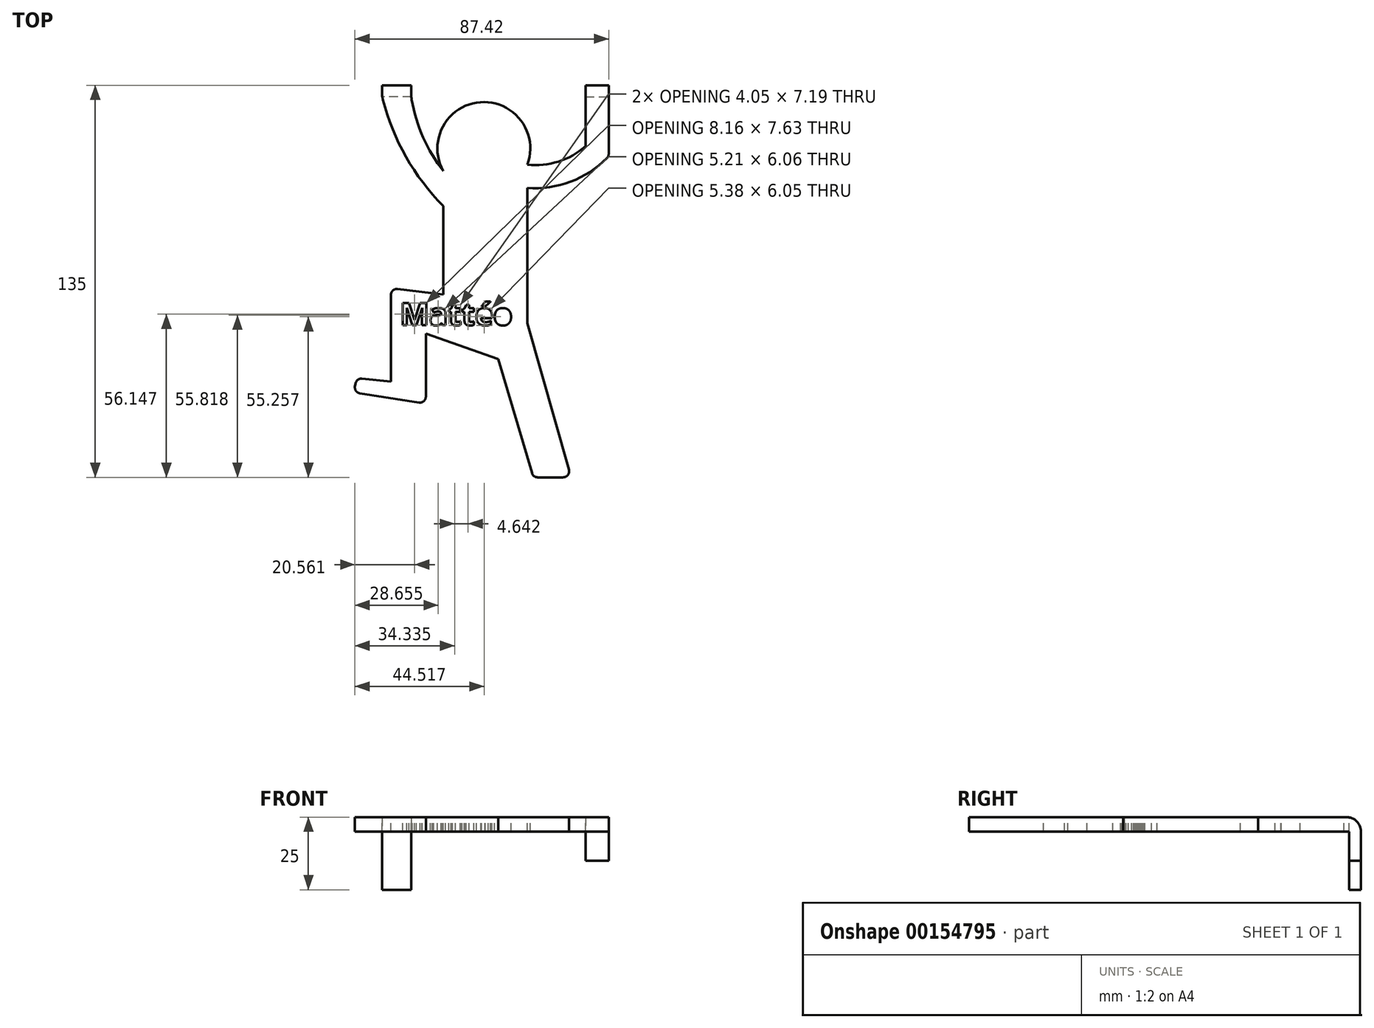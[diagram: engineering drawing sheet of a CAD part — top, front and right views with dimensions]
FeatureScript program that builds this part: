
annotation { "Feature Type Name" : "Feature", "Feature Type Description" : "" }
export const myFeature = defineFeature(function(context is Context, id is Id, definition is map)
    precondition{}
    {
        {
            var Q0;
            Q0=qCreatedBy(makeId("Top.planeOp"),FACE);
            var sketch = newSketch(context, id + "F0", { "sketchPlane" : qUnion([Q0])});
            skCircle(sketch, "E0", {"center": v(0, 33.2) * mm, "radius": 16 * mm});
            skLineSegment(sketch, "E1", {"start": v(15, 19.62) * mm, "end": v(15, -26.94) * mm});
            skLineSegment(sketch, "E2", {"start": v(15, -26.94) * mm, "end": v(30, -80) * mm});
            skLineSegment(sketch, "E3", {"start": v(30, -80) * mm, "end": v(17, -80) * mm});
            skLineSegment(sketch, "E4", {"start": v(17, -80) * mm, "end": v(5, -39.34) * mm});
            skLineSegment(sketch, "E5", {"start": v(5, -39.34) * mm, "end": v(-20, -30.5) * mm});
            skLineSegment(sketch, "E6", {"start": v(-20, -30.5) * mm, "end": v(-20, -54.61) * mm});
            skLineSegment(sketch, "E7", {"start": v(-20, -54.61) * mm, "end": v(-44.7, -50.77) * mm});
            skLineSegment(sketch, "E8", {"start": v(-44.7, -50.77) * mm, "end": v(-43.94, -45.83) * mm});
            skLineSegment(sketch, "E9", {"start": v(-43.94, -45.83) * mm, "end": v(-32, -47.08) * mm});
            skLineSegment(sketch, "E10", {"start": v(-32, -47.08) * mm, "end": v(-32, -14.9) * mm});
            skLineSegment(sketch, "E11", {"start": v(-32, -14.9) * mm, "end": v(-14, -17.13) * mm});
            skLineSegment(sketch, "E12", {"start": v(-14, -17.13) * mm, "end": v(-14, 13.45) * mm});
            skLineSegment(sketch, "E13.bottom", {"start": v(35, 55) * mm, "end": v(43, 55) * mm});
            skLineSegment(sketch, "E13.top", {"start": v(35, 51) * mm, "end": v(43, 51) * mm});
            skLineSegment(sketch, "E13.left", {"start": v(35, 55) * mm, "end": v(35, 51) * mm});
            skLineSegment(sketch, "E13.right", {"start": v(43, 55) * mm, "end": v(43, 51) * mm});
            skLineSegment(sketch, "E14.bottom", {"start": v(-25, 55) * mm, "end": v(-35, 55) * mm});
            skLineSegment(sketch, "E14.top", {"start": v(-25, 51) * mm, "end": v(-35, 51) * mm});
            skLineSegment(sketch, "E14.left", {"start": v(-25, 55) * mm, "end": v(-25, 51) * mm});
            skLineSegment(sketch, "E14.right", {"start": v(-35, 55) * mm, "end": v(-35, 51) * mm});
            skPoint(sketch, "E15", {"position": v(-14, 25.45) * mm});
            skPoint(sketch, "E16", {"position": v(15, 19.62) * mm});
            skPoint(sketch, "E17", {"position": v(15, 27.62) * mm});
            skArc(sketch, "E18", {"start": v(-25, 51) * mm, "mid": v(-21.14, 37.52) * mm, "end": v(-14, 25.45) * mm});
            skArc(sketch, "E19", {"start": v(-35, 51) * mm, "mid": v(-27.07, 30.78) * mm, "end": v(-14, 13.45) * mm});
            skLineSegment(sketch, "E20", {"start": v(43, 51) * mm, "end": v(43, 30.54) * mm});
            skLineSegment(sketch, "E21", {"start": v(35, 51) * mm, "end": v(35, 34) * mm});
            skArc(sketch, "E22", {"start": v(15, 19.62) * mm, "mid": v(30.23, 21.92) * mm, "end": v(43, 30.54) * mm});
            skArc(sketch, "E23", {"start": v(15, 27.62) * mm, "mid": v(25.67, 28.7) * mm, "end": v(35, 34) * mm});
            skText(sketch, "E24", { "text": "Mattéo", "fontName": "OpenSans-Bold.ttf"});
            const initialGuessF0  = {"E24": [-0.0289, -0.02767, 1, 0, 0.0077]};
            skSetInitialGuess(sketch, initialGuessF0);
            skSolve(sketch);
        }
        {
            var Q0;
            Q0=makeQuery(id+"F0.imprint","IMPRINT",FACE,{"disambiguationData":[TD([[makeQuery(id+"F0.imprint","IMPRINT",EDGE,{"derivedFrom":sQuery(id+"F0.wireOp",EDGE,"E1")}),-1.0]])]});
            var Q1;
            {var subQ0=sQuery(id+"F0.wireOp",EDGE,"E0");var subQ1=makeQuery(id+"F0.imprint","INTERSECT",VERTEX,{"derivedFrom":[subQ0,sQuery(id+"F0.wireOp",EDGE,"E18")]});Q1=makeQuery(id+"F0.imprint","IMPRINT",FACE,{"disambiguationData":[TD([[makeQuery(id+"F0.imprint","IMPRINT",EDGE,{"disambiguationData":[TD([[subQ1,-1.0]])],"derivedFrom":subQ0}),1.0]])]});}
            extrude(context, id + "F1", {"entities" : qUnion([Q0, Q1]), "oppositeDirection" : true, "depth" : 5 * mm});
        }
        {
            var Q0;
            Q0=makeQuery(id+"F0.imprint","IMPRINT",FACE,{"disambiguationData":[TD([[makeQuery(id+"F0.imprint","IMPRINT",EDGE,{"derivedFrom":sQuery(id+"F0.wireOp",EDGE,"E14.bottom")}),1.0]])]});
            extrude(context, id + "F2", {"entities" : qUnion([Q0]), "operationType" : NewBodyOperationType.ADD, "oppositeDirection" : true, "depth" : 25 * mm});
        }
        {
            var Q0;
            Q0=makeQuery(id+"F0.imprint","IMPRINT",FACE,{"disambiguationData":[TD([[makeQuery(id+"F0.imprint","IMPRINT",EDGE,{"derivedFrom":sQuery(id+"F0.wireOp",EDGE,"E13.bottom")}),-1.0]])]});
            extrude(context, id + "F3", {"entities" : qUnion([Q0]), "operationType" : NewBodyOperationType.ADD, "oppositeDirection" : true, "depth" : 15 * mm});
        }
        {
            var Q0;
            Q0=makeQuery(id+"F2.opExtrude","CAP_EDGE",EDGE,{"disambiguationData":[OSD([sQuery(id+"F0.wireOp",EDGE,"E14.bottom")])],"isStart":true});
            var Q1;
            Q1=makeQuery(id+"F3.opExtrude","CAP_EDGE",EDGE,{"disambiguationData":[OSD([sQuery(id+"F0.wireOp",EDGE,"E13.bottom")])],"isStart":true});
            fillet(context, id + "F4", {"entities" : qUnion([Q0, Q1]), "radius" : 5 * mm, "tangentPropagation" : true, "allowEdgeOverflow" : false});
        }
        {
            var Q0;
            Q0=makeQuery(id+"F1.opExtrude","SWEPT_EDGE",EDGE,{"disambiguationData":[OSD([sQuery(id+"F0.wireOp",EDGE,"E8"),sQuery(id+"F0.wireOp",EDGE,"E9")])]});
            var Q1;
            Q1=makeQuery(id+"F1.opExtrude","SWEPT_EDGE",EDGE,{"disambiguationData":[OSD([sQuery(id+"F0.wireOp",EDGE,"E7"),sQuery(id+"F0.wireOp",EDGE,"E8")])]});
            var Q2;
            Q2=makeQuery(id+"F1.opExtrude","SWEPT_EDGE",EDGE,{"disambiguationData":[OSD([sQuery(id+"F0.wireOp",EDGE,"E3"),sQuery(id+"F0.wireOp",EDGE,"E4")])]});
            var Q3;
            Q3=makeQuery(id+"F1.opExtrude","SWEPT_EDGE",EDGE,{"disambiguationData":[OSD([sQuery(id+"F0.wireOp",EDGE,"E2"),sQuery(id+"F0.wireOp",EDGE,"E3")])]});
            var Q4;
            Q4=makeQuery(id+"F1.opExtrude","SWEPT_EDGE",EDGE,{"disambiguationData":[OSD([sQuery(id+"F0.wireOp",EDGE,"E6"),sQuery(id+"F0.wireOp",EDGE,"E7")])]});
            var Q5;
            Q5=makeQuery(id+"F1.opExtrude","SWEPT_EDGE",EDGE,{"disambiguationData":[OSD([sQuery(id+"F0.wireOp",EDGE,"E10"),sQuery(id+"F0.wireOp",EDGE,"E11")])]});
            var Q6;
            Q6=makeQuery(id+"F1.opExtrude","SWEPT_EDGE",EDGE,{"disambiguationData":[OSD([sQuery(id+"F0.wireOp",EDGE,"E20"),sQuery(id+"F0.wireOp",EDGE,"E22")])]});
            fillet(context, id + "F5", {"entities" : qUnion([Q0, Q1, Q2, Q3, Q4, Q5, Q6]), "radius" : 2 * mm, "tangentPropagation" : true, "allowEdgeOverflow" : false});
        }
    });
